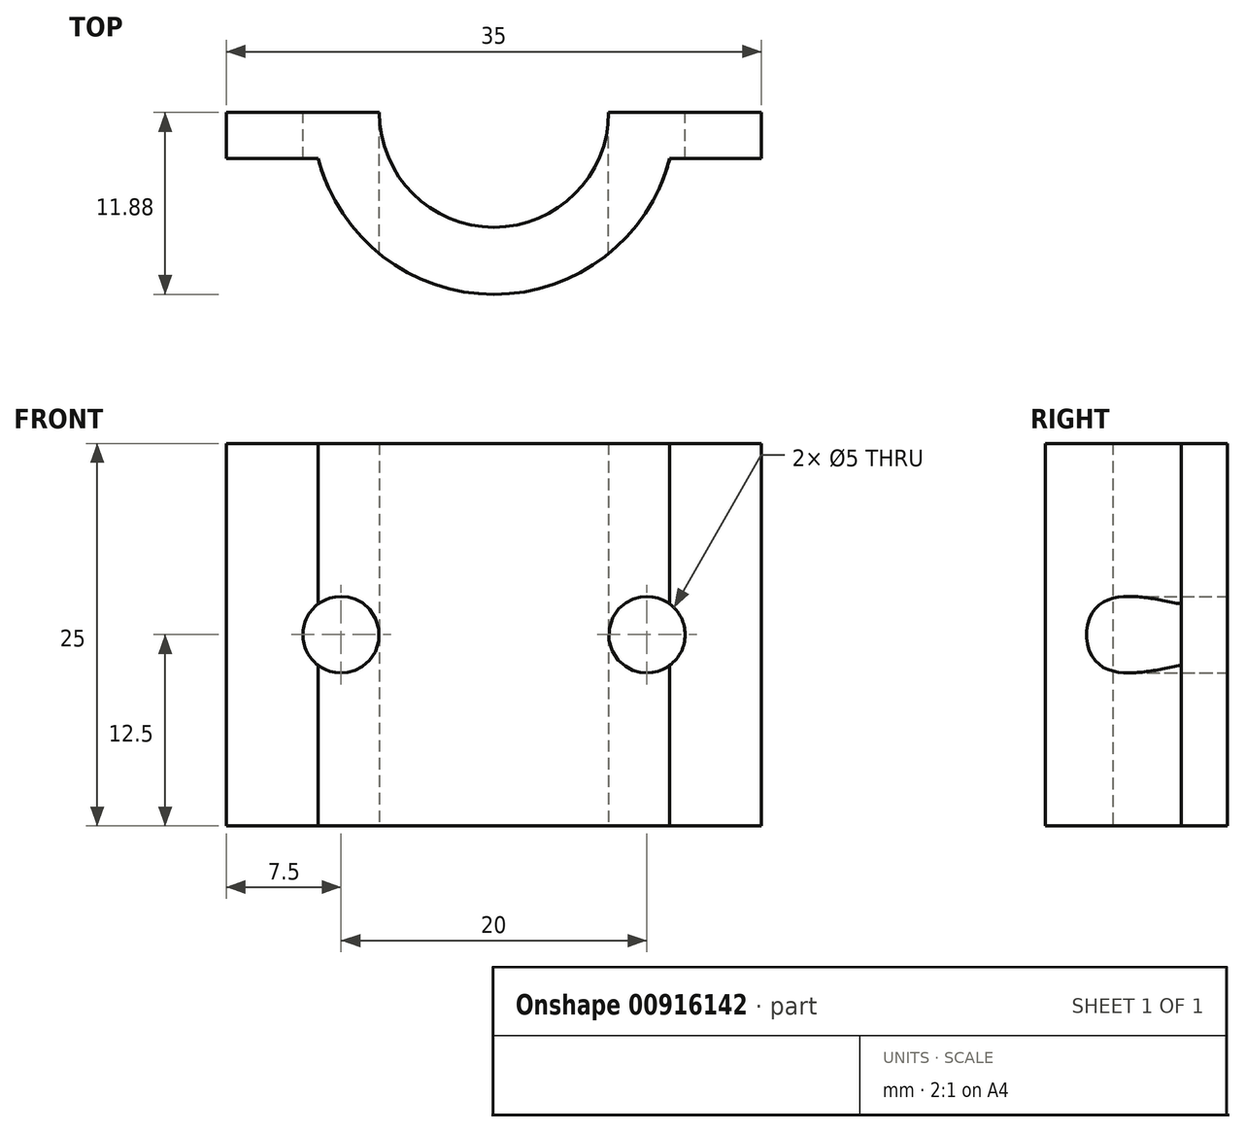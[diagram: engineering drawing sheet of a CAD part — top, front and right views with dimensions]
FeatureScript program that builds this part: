
annotation { "Feature Type Name" : "Feature", "Feature Type Description" : "" }
export const myFeature = defineFeature(function(context is Context, id is Id, definition is map)
    precondition{}
    {
        {
            var Q0;
            Q0=qCreatedBy(makeId("Top.planeOp"),FACE);
            var sketch = newSketch(context, id + "F0", { "sketchPlane" : qUnion([Q0])});
            skLineSegment(sketch, "E0", {"start": v(-17.5, 0) * mm, "end": v(-7.5, 0) * mm});
            skLineSegment(sketch, "E1", {"start": v(7.5, 0) * mm, "end": v(17.5, 0) * mm});
            skArc(sketch, "E2", {"start": v(7.5, 0) * mm, "mid": v(0, -7.5) * mm, "end": v(-7.5, 0) * mm});
            skLineSegment(sketch, "E3", {"start": v(17.5, 0) * mm, "end": v(17.5, -3) * mm});
            skLineSegment(sketch, "E4", {"start": v(17.5, -3) * mm, "end": v(11.5, -3) * mm});
            skLineSegment(sketch, "E5", {"start": v(-17.5, 0) * mm, "end": v(-17.5, -3) * mm});
            skLineSegment(sketch, "E6", {"start": v(-17.5, -3) * mm, "end": v(-11.5, -3) * mm});
            skArc(sketch, "E7", {"start": v(-11.5, -3) * mm, "mid": v(0, -11.88) * mm, "end": v(11.5, -3) * mm});
            skSolve(sketch);
        }
        {
            var Q0;
            Q0 = qSketchRegion(id + "F0", true);
            extrude(context, id + "F1", {"entities" : qUnion([Q0]), "depth" : 25 * mm, "offsetDistance" : 25 * mm});
        }
        {
            var Q0;
            Q0=makeQuery(id+"F1.opExtrude","SWEPT_FACE",FACE,{"disambiguationData":[OSD([sQuery(id+"F0.wireOp",EDGE,"E1")])]});
            var sketch = newSketch(context, id + "F2", { "sketchPlane" : qUnion([Q0])});
            skCircle(sketch, "E8", {"center": v(-10, 12.5) * mm, "radius": 2.5 * mm});
            skCircle(sketch, "E9", {"center": v(10, 12.5) * mm, "radius": 2.5 * mm});
            skSolve(sketch);
        }
        {
            var Q0;
            Q0=sQuery(id+"F2.wireOp",VERTEX,"E8.center");
            var Q1;
            Q1=sQuery(id+"F2.wireOp",VERTEX,"E9.center");
            var Q2;
            Q2=makeQuery(id+"F1.opExtrude","SWEPT_BODY",BODY,{"disambiguationData":[OSD([sQuery(id+"F0.wireOp",EDGE,"E0"),sQuery(id+"F0.wireOp",EDGE,"E1"),sQuery(id+"F0.wireOp",EDGE,"E2"),sQuery(id+"F0.wireOp",EDGE,"E3"),sQuery(id+"F0.wireOp",EDGE,"E4"),sQuery(id+"F0.wireOp",EDGE,"E5"),sQuery(id+"F0.wireOp",EDGE,"E6"),sQuery(id+"F0.wireOp",EDGE,"E7")])]});
            hole(context, id + "F3", {"style" : HoleStyle.SIMPLE, "endStyle" : HoleEndStyle.THROUGH, "holeDiameter" : 5 * mm, "majorDiameter" : 5 * mm, "isTappedThrough" : true, "tappedDepth" : 12 * mm, "tapClearance" : 3, "locations" : qUnion([Q0, Q1]), "scope" : qUnion([Q2])});
        }
    });
